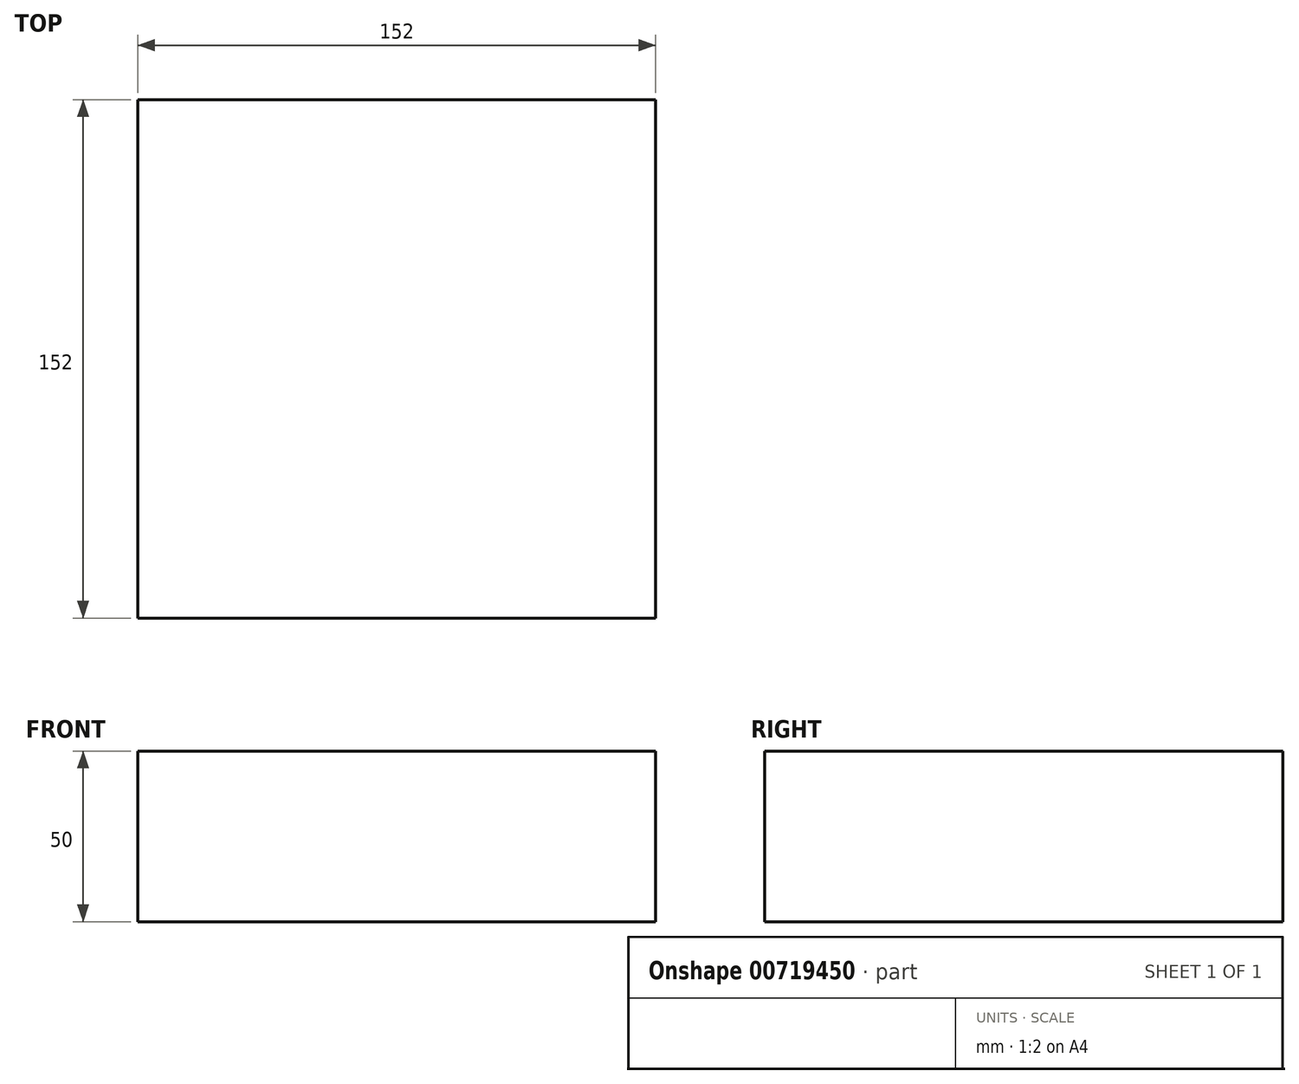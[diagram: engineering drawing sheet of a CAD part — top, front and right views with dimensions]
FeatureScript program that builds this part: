
annotation { "Feature Type Name" : "Feature", "Feature Type Description" : "" }
export const myFeature = defineFeature(function(context is Context, id is Id, definition is map)
    precondition{}
    {
        {
            var Q0;
            Q0=qCreatedBy(makeId("Top.planeOp"),FACE);
            var sketch = newSketch(context, id + "F0", { "sketchPlane" : qUnion([Q0])});
            skLineSegment(sketch, "E0.bottom", {"start": v(-76, 76) * mm, "end": v(76, 76) * mm});
            skLineSegment(sketch, "E0.top", {"start": v(-76, -76) * mm, "end": v(76, -76) * mm});
            skLineSegment(sketch, "E0.left", {"start": v(-76, 76) * mm, "end": v(-76, -76) * mm});
            skLineSegment(sketch, "E0.right", {"start": v(76, 76) * mm, "end": v(76, -76) * mm});
            skPoint(sketch, "E1", {"position": v(0, 0) * mm});
            skSolve(sketch);
        }
        {
            var Q0;
            Q0=makeQuery(id+"F0.imprint","IMPRINT",FACE,{"disambiguationData":[TD([[makeQuery(id+"F0.imprint","IMPRINT",EDGE,{"derivedFrom":sQuery(id+"F0.wireOp",EDGE,"E0.bottom")}),-1.0]])]});
            extrude(context, id + "F1", {"entities" : qUnion([Q0]), "depth" : 50 * mm, "offsetDistance" : 25 * mm});
        }
    });
